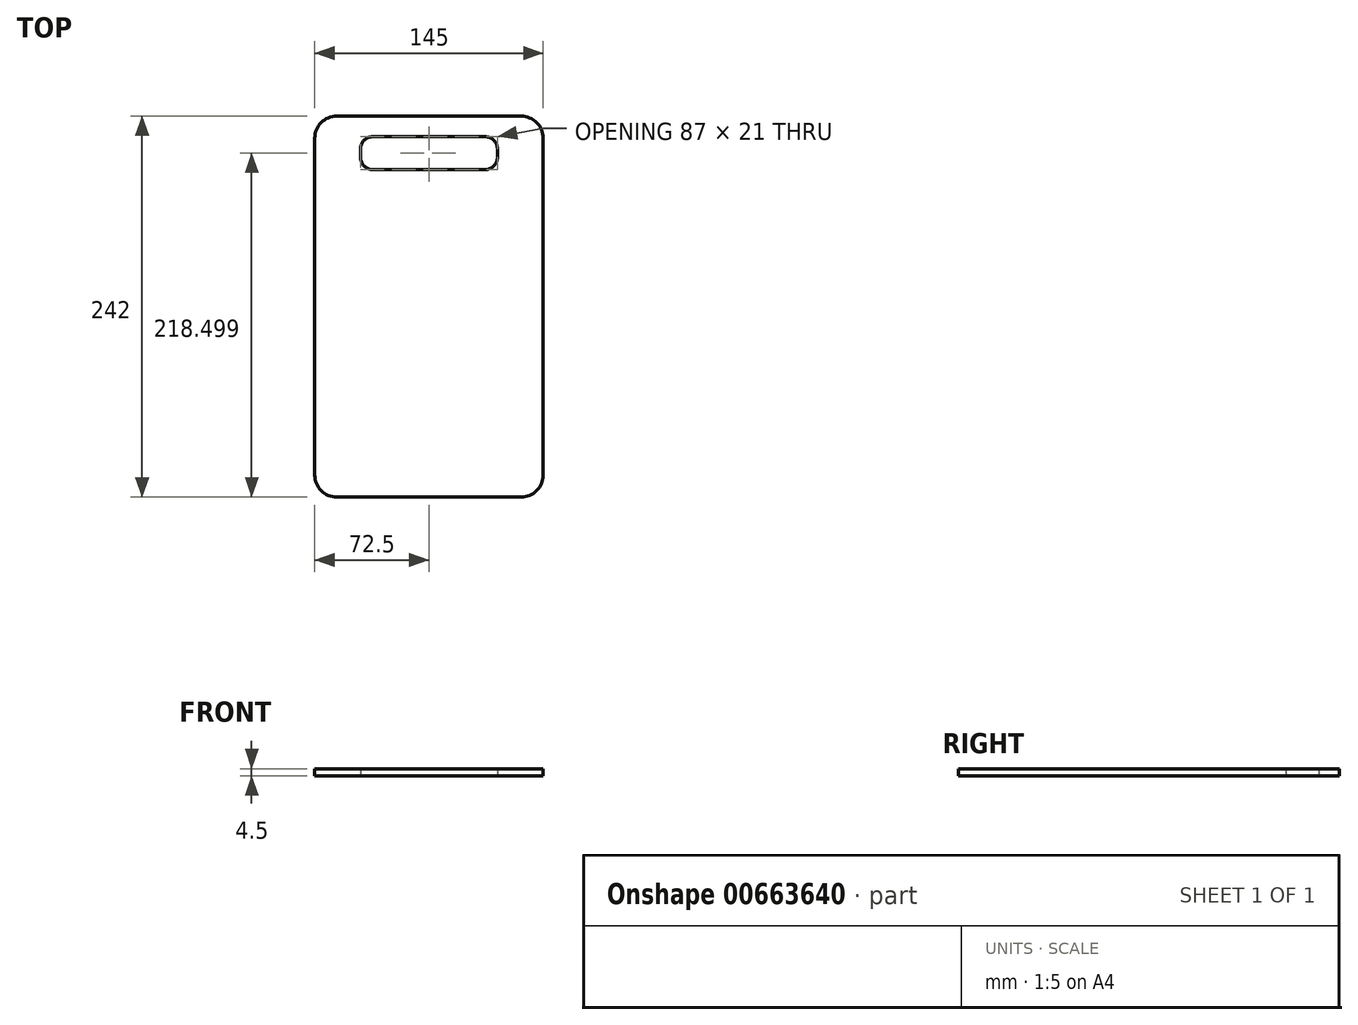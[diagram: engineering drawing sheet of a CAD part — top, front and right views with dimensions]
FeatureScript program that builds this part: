
annotation { "Feature Type Name" : "Feature", "Feature Type Description" : "" }
export const myFeature = defineFeature(function(context is Context, id is Id, definition is map)
    precondition{}
    {
        {
            var Q0;
            Q0=qCreatedBy(makeId("Top.planeOp"),FACE);
            var sketch = newSketch(context, id + "F0", { "sketchPlane" : qUnion([Q0])});
            skLineSegment(sketch, "E0.bottom", {"start": v(-40.62, 138.3) * mm, "end": v(76.38, 138.3) * mm});
            skLineSegment(sketch, "E0.top", {"start": v(-40.62, -103.7) * mm, "end": v(76.38, -103.7) * mm});
            skLineSegment(sketch, "E0.left", {"start": v(-54.62, 124.3) * mm, "end": v(-54.62, -89.7) * mm});
            skLineSegment(sketch, "E0.right", {"start": v(90.38, 124.3) * mm, "end": v(90.38, -89.7) * mm});
            skPoint(sketch, "E1.visualSharp", {"position": v(-54.62, 138.3) * mm});
            skArc(sketch, "E1.filletArc", {"start": v(-40.62, 138.3) * mm, "mid": v(-50.52, 134.2) * mm, "end": v(-54.62, 124.3) * mm});
            skPoint(sketch, "E2.visualSharp", {"position": v(90.38, 138.3) * mm});
            skArc(sketch, "E2.filletArc", {"start": v(90.38, 124.3) * mm, "mid": v(86.28, 134.2) * mm, "end": v(76.38, 138.3) * mm});
            skPoint(sketch, "E3.visualSharp", {"position": v(90.38, -103.7) * mm});
            skArc(sketch, "E3.filletArc", {"start": v(76.38, -103.7) * mm, "mid": v(86.28, -99.6) * mm, "end": v(90.38, -89.7) * mm});
            skPoint(sketch, "E4.visualSharp", {"position": v(-54.62, -103.7) * mm});
            skArc(sketch, "E4.filletArc", {"start": v(-54.62, -89.7) * mm, "mid": v(-50.52, -99.6) * mm, "end": v(-40.62, -103.7) * mm});
            skLineSegment(sketch, "E5.bottom", {"start": v(-17.62, 125.3) * mm, "end": v(53.38, 125.3) * mm});
            skLineSegment(sketch, "E5.top", {"start": v(-17.62, 104.3) * mm, "end": v(53.38, 104.3) * mm});
            skLineSegment(sketch, "E5.left", {"start": v(-25.62, 117.3) * mm, "end": v(-25.62, 112.3) * mm});
            skLineSegment(sketch, "E5.right", {"start": v(61.38, 117.3) * mm, "end": v(61.38, 112.3) * mm});
            skPoint(sketch, "E6", {"position": v(0, 138.3) * mm});
            skPoint(sketch, "E7", {"position": v(17.88, 104.3) * mm});
            skPoint(sketch, "E8.visualSharp", {"position": v(-25.62, 125.3) * mm});
            skArc(sketch, "E8.filletArc", {"start": v(-17.62, 125.3) * mm, "mid": v(-23.28, 122.97) * mm, "end": v(-25.62, 117.3) * mm});
            skPoint(sketch, "E9.visualSharp", {"position": v(-25.62, 104.3) * mm});
            skArc(sketch, "E9.filletArc", {"start": v(-25.62, 112.3) * mm, "mid": v(-23.28, 106.65) * mm, "end": v(-17.62, 104.3) * mm});
            skPoint(sketch, "E10.visualSharp", {"position": v(61.38, 104.3) * mm});
            skArc(sketch, "E10.filletArc", {"start": v(53.38, 104.3) * mm, "mid": v(59.04, 106.65) * mm, "end": v(61.38, 112.3) * mm});
            skPoint(sketch, "E11.visualSharp", {"position": v(61.38, 125.3) * mm});
            skArc(sketch, "E11.filletArc", {"start": v(61.38, 117.3) * mm, "mid": v(59.04, 122.97) * mm, "end": v(53.38, 125.3) * mm});
            skSolve(sketch);
        }
        {
            var Q0;
            Q0=qSketchRegion(id+"F0",true);
            extrude(context, id + "F1", {"entities" : qUnion([Q0]), "depth" : 4.5 * mm, "offsetDistance" : 25 * mm});
        }
    });
